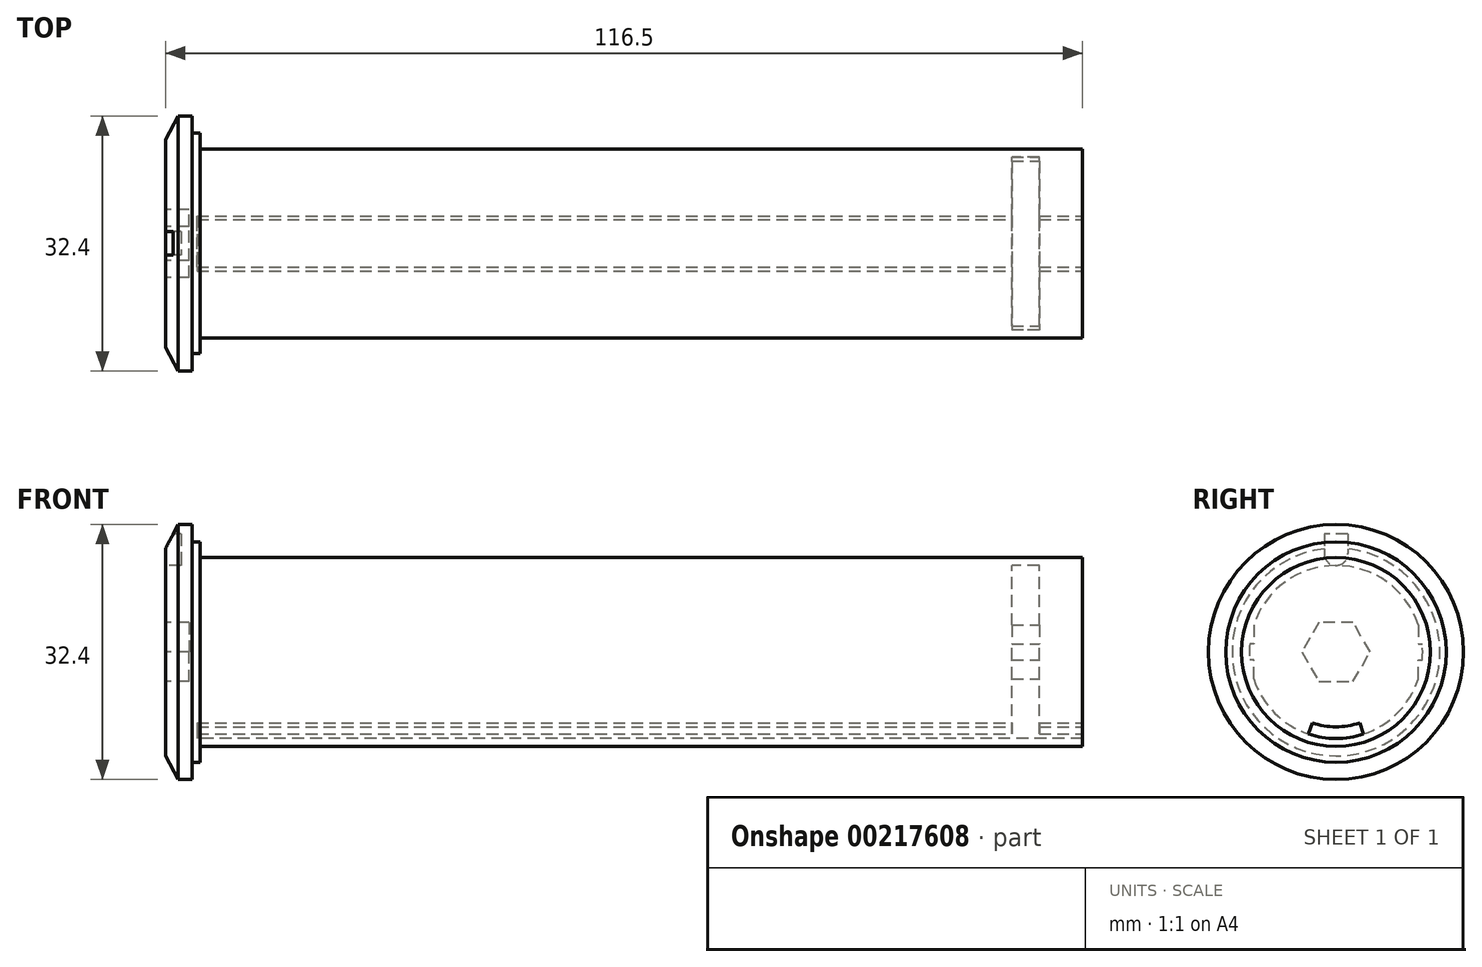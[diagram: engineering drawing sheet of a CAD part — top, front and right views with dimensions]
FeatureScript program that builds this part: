
annotation { "Feature Type Name" : "Feature", "Feature Type Description" : "" }
export const myFeature = defineFeature(function(context is Context, id is Id, definition is map)
    precondition{}
    {
        {
            var Q0;
            Q0=qCreatedBy(makeId("Front.planeOp"),FACE);
            var sketch = newSketch(context, id + "F0", { "sketchPlane" : qUnion([Q0])});
            skLineSegment(sketch, "E0", {"start": v(-68.2, 0) * mm, "end": v(74.54, 0) * mm, "construction": true});
            skLineSegment(sketch, "E1", {"start": v(-50, 0) * mm, "end": v(-50, 13.2) * mm});
            skLineSegment(sketch, "E2", {"start": v(-50, 13.2) * mm, "end": v(-48.4, 16.2) * mm});
            skLineSegment(sketch, "E3", {"start": v(-48.4, 16.2) * mm, "end": v(-46.6, 16.2) * mm});
            skLineSegment(sketch, "E4", {"start": v(-45.6, 12) * mm, "end": v(66.5, 12) * mm});
            skLineSegment(sketch, "E5", {"start": v(66.5, 12) * mm, "end": v(66.5, 11) * mm});
            skLineSegment(sketch, "E6", {"start": v(66.5, 11) * mm, "end": v(-46, 11) * mm});
            skLineSegment(sketch, "E7", {"start": v(-46, 11) * mm, "end": v(-46, 0) * mm});
            skLineSegment(sketch, "E8", {"start": v(-50, 0) * mm, "end": v(-46, 0) * mm});
            skLineSegment(sketch, "E9", {"start": v(-46.6, 16.2) * mm, "end": v(-46.6, 14) * mm});
            skLineSegment(sketch, "E10", {"start": v(-46.6, 14) * mm, "end": v(-45.6, 14) * mm});
            skLineSegment(sketch, "E11", {"start": v(-45.6, 14) * mm, "end": v(-45.6, 12) * mm});
            skSolve(sketch);
        }
        {
            var Q0;
            Q0 = qSketchRegion(id + "F0", true);
            var Q1;
            Q1=sQuery(id+"F0.wireOp",EDGE,"E0");
            revolve(context, id + "F1", {"entities" : qUnion([Q0]), "axis" : qUnion([Q1]), "revolveType" : RevolveType.FULL});
        }
        {
            var Q0;
            Q0=makeQuery(id+"F1.opRevolve","SWEPT_FACE",FACE,{"disambiguationData":[OSD([sQuery(id+"F0.wireOp",EDGE,"E5")])]});
            var sketch = newSketch(context, id + "F2", { "sketchPlane" : qUnion([Q0])});
            skLineSegment(sketch, "E12", {"start": v(10.95, 1) * mm, "end": v(11.25, 1) * mm});
            skLineSegment(sketch, "E13", {"start": v(11.25, 1) * mm, "end": v(11.25, -1) * mm});
            skLineSegment(sketch, "E14", {"start": v(11.25, -1) * mm, "end": v(10.95, -1) * mm});
            skLineSegment(sketch, "E15", {"start": v(-10.95, 1) * mm, "end": v(-11.25, 1) * mm});
            skLineSegment(sketch, "E16", {"start": v(-11.25, 1) * mm, "end": v(-11.25, -1) * mm});
            skLineSegment(sketch, "E17", {"start": v(-11.25, -1) * mm, "end": v(-10.95, -1) * mm});
            skLineSegment(sketch, "E18", {"start": v(-10.45, 3.42) * mm, "end": v(-10.45, 1) * mm});
            skLineSegment(sketch, "E19", {"start": v(-10.45, 1) * mm, "end": v(-10.95, 1) * mm});
            skLineSegment(sketch, "E20", {"start": v(-10.45, -3.42) * mm, "end": v(-10.45, -1) * mm});
            skLineSegment(sketch, "E21", {"start": v(-10.45, -1) * mm, "end": v(-10.95, -1) * mm});
            skLineSegment(sketch, "E22", {"start": v(10.45, 3.42) * mm, "end": v(10.45, 1) * mm});
            skLineSegment(sketch, "E23", {"start": v(10.45, 1) * mm, "end": v(10.95, 1) * mm});
            skLineSegment(sketch, "E24", {"start": v(10.45, -3.42) * mm, "end": v(10.45, -1) * mm});
            skLineSegment(sketch, "E25", {"start": v(10.45, -1) * mm, "end": v(10.95, -1) * mm});
            skSolve(sketch);
        }
        {
            var Q0;
            {var subQ0=sQuery(id+"F2.wireOp",EDGE,"E15");Q0=makeQuery(id+"F2.imprint","IMPRINT",FACE,{"disambiguationData":[TD([[makeQuery(id+"F2.imprint","IMPRINT",EDGE,{"derivedFrom":subQ0}),1.0]])]});}
            var Q1;
            {var subQ0=sQuery(id+"F2.wireOp",EDGE,"E12");Q1=makeQuery(id+"F2.imprint","IMPRINT",FACE,{"disambiguationData":[TD([[makeQuery(id+"F2.imprint","IMPRINT",EDGE,{"derivedFrom":subQ0}),-1.0]])]});}
            extrude(context, id + "F3", {"entities" : qUnion([Q0, Q1]), "operationType" : NewBodyOperationType.REMOVE, "oppositeDirection" : true, "depth" : 112 * mm});
        }
        {
            var Q0;
            {var subQ5=sQuery(id+"F2.wireOp",EDGE,"E12");Q0=makeQuery(id+"F2.imprint","IMPRINT",FACE,{"disambiguationData":[TD([[makeQuery(id+"F2.imprint","IMPRINT",EDGE,{"derivedFrom":subQ5}),1.0]])]});}
            var sketch = newSketch(context, id + "F4", { "sketchPlane" : qUnion([Q0])});
            skLineSegment(sketch, "E26", {"start": v(-3.5, 10.43) * mm, "end": v(-3.02, 9) * mm});
            skLineSegment(sketch, "E27", {"start": v(3.5, 10.43) * mm, "end": v(3.02, 9) * mm});
            skArc(sketch, "E28", {"start": v(3.02, 9) * mm, "mid": v(0, 9.5) * mm, "end": v(-3.02, 9) * mm});
            skArc(sketch, "E29.MirrorCS", {"start": v(3.02, -9) * mm, "mid": v(0, -9.5) * mm, "end": v(-3.02, -9) * mm});
            skLineSegment(sketch, "E30.MirrorCS", {"start": v(-3.5, -10.43) * mm, "end": v(-3.02, -9) * mm});
            skLineSegment(sketch, "E31.MirrorCS", {"start": v(3.5, -10.43) * mm, "end": v(3.02, -9) * mm});
            skSolve(sketch);
        }
        {
            var Q0;
            {var subQ0=sQuery(id+"F4.wireOp",EDGE,"E26");Q0=makeQuery(id+"F4.imprint","IMPRINT",FACE,{"disambiguationData":[TD([[makeQuery(id+"F4.imprint","IMPRINT",EDGE,{"derivedFrom":subQ0}),1.0]])]});}
            var Q1;
            Q1=makeQuery(id+"F4.imprint","IMPRINT",FACE,{"disambiguationData":[TD([[makeQuery(id+"F4.imprint","IMPRINT",EDGE,{"derivedFrom":sQuery(id+"F4.wireOp",EDGE,"E29.MirrorCS")}),1.0]])]});
            var Q2;
            {var subQ5=sQuery(id+"F2.wireOp",EDGE,"E12");var subQ10=makeQuery(id+"F3.boolean.opBoolean","COPY",EDGE,{"derivedFrom":makeQuery(id+"F3.opExtrude","CAP_EDGE",EDGE,{"disambiguationData":[OSD([subQ5])],"isStart":true})});Q2=makeQuery(id+"F4.imprint","IMPRINT",FACE,{"disambiguationData":[TD([[makeQuery(id+"F4.imprint","IMPRINT",EDGE,{"derivedFrom":subQ10}),1.0]])]});}
            var Q3;
            Q3=makeQuery(id+"F1.opRevolve","SWEPT_FACE",FACE,{"disambiguationData":[OSD([sQuery(id+"F0.wireOp",EDGE,"E7")])]});
            extrude(context, id + "F5", {"entities" : qUnion([Q0, Q1, Q2]), "operationType" : NewBodyOperationType.ADD, "endBound" : BoundingType.UP_TO_SURFACE, "oppositeDirection" : true, "endBoundEntityFace" : qUnion([Q3]), "depth" : 25 * mm});
        }
        {
            var Q0;
            Q0=makeQuery(id+"F1.opRevolve","SWEPT_FACE",FACE,{"disambiguationData":[OSD([sQuery(id+"F0.wireOp",EDGE,"E1")])]});
            var sketch = newSketch(context, id + "F6", { "sketchPlane" : qUnion([Q0])});
            skCircle(sketch, "E32.cCircle", {"center": v(0, 0) * mm, "radius": 4.33 * mm, "construction": true});
            skLineSegment(sketch, "E32.0", {"start": v(-2.17, -3.75) * mm, "end": v(-4.33, 0) * mm});
            skLineSegment(sketch, "E32.1", {"start": v(-4.33, 0) * mm, "end": v(-2.17, 3.75) * mm});
            skLineSegment(sketch, "E32.2", {"start": v(-2.17, 3.75) * mm, "end": v(2.17, 3.75) * mm});
            skLineSegment(sketch, "E32.3", {"start": v(2.17, 3.75) * mm, "end": v(4.33, 0) * mm});
            skLineSegment(sketch, "E32.4", {"start": v(4.33, 0) * mm, "end": v(2.17, -3.75) * mm});
            skLineSegment(sketch, "E32.5", {"start": v(2.17, -3.75) * mm, "end": v(-2.17, -3.75) * mm});
            skSolve(sketch);
        }
        {
            var Q0;
            Q0=makeQuery(id+"F6.imprint","IMPRINT",FACE,{"disambiguationData":[TD([[makeQuery(id+"F6.imprint","IMPRINT",EDGE,{"derivedFrom":sQuery(id+"F6.wireOp",EDGE,"E32.0")}),-1.0]])]});
            extrude(context, id + "F7", {"entities" : qUnion([Q0]), "operationType" : NewBodyOperationType.REMOVE, "oppositeDirection" : true, "depth" : 3 * mm});
        }
        {
            var Q0;
            Q0=makeQuery(id+"F1.opRevolve","SWEPT_FACE",FACE,{"disambiguationData":[OSD([sQuery(id+"F0.wireOp",EDGE,"E1")])]});
            var sketch = newSketch(context, id + "F8", { "sketchPlane" : qUnion([Q0])});
            skLineSegment(sketch, "E33", {"start": v(-1.5, 15) * mm, "end": v(-1.5, 12.5) * mm});
            skLineSegment(sketch, "E34", {"start": v(-1.5, 15) * mm, "end": v(1.5, 15) * mm});
            skLineSegment(sketch, "E35", {"start": v(1.5, 15) * mm, "end": v(1.5, 12.5) * mm});
            skArc(sketch, "E36", {"start": v(-1.5, 12.5) * mm, "mid": v(0, 11) * mm, "end": v(1.5, 12.5) * mm});
            skPoint(sketch, "E37", {"position": v(0, 15) * mm});
            skSolve(sketch);
        }
        {
            var Q0;
            Q0 = qSketchRegion(id + "F8", true);
            extrude(context, id + "F9", {"entities" : qUnion([Q0]), "operationType" : NewBodyOperationType.REMOVE, "oppositeDirection" : true, "depth" : 2 * mm});
        }
        {
            var Q0;
            Q0=qCreatedBy(makeId("Right.planeOp"),FACE);
            var sketch = newSketch(context, id + "F10", { "sketchPlane" : qUnion([Q0])});
            skCircle(sketch, "E38", {"center": v(0, 0) * mm, "radius": 11 * mm});
            skSolve(sketch);
        }
        {
            var Q0;
            Q0 = qSketchRegion(id + "F10", true);
            extrude(context, id + "F11", {"entities" : qUnion([Q0]), "operationType" : NewBodyOperationType.REMOVE, "depth" : 61 * mm, "hasSecondDirection" : true, "secondDirectionOppositeDirection" : false, "secondDirectionDepth" : 57.5 * mm});
        }
        {
            var Q0;
            {var subQ0=sQuery(id+"F2.wireOp",EDGE,"E22");Q0=makeQuery(id+"F2.imprint","IMPRINT",FACE,{"disambiguationData":[TD([[makeQuery(id+"F2.imprint","IMPRINT",EDGE,{"derivedFrom":subQ0}),1.0]])]});}
            var Q1;
            {var subQ0=sQuery(id+"F2.wireOp",EDGE,"E24");Q1=makeQuery(id+"F2.imprint","IMPRINT",FACE,{"disambiguationData":[TD([[makeQuery(id+"F2.imprint","IMPRINT",EDGE,{"derivedFrom":subQ0}),-1.0]])]});}
            var Q2;
            {var subQ0=sQuery(id+"F2.wireOp",EDGE,"E20");Q2=makeQuery(id+"F2.imprint","IMPRINT",FACE,{"disambiguationData":[TD([[makeQuery(id+"F2.imprint","IMPRINT",EDGE,{"derivedFrom":subQ0}),1.0]])]});}
            var Q3;
            {var subQ0=sQuery(id+"F2.wireOp",EDGE,"E18");Q3=makeQuery(id+"F2.imprint","IMPRINT",FACE,{"disambiguationData":[TD([[makeQuery(id+"F2.imprint","IMPRINT",EDGE,{"derivedFrom":subQ0}),-1.0]])]});}
            extrude(context, id + "F12", {"entities" : qUnion([Q0, Q1, Q2, Q3]), "operationType" : NewBodyOperationType.ADD, "oppositeDirection" : true, "depth" : 100 * mm});
        }
    });
